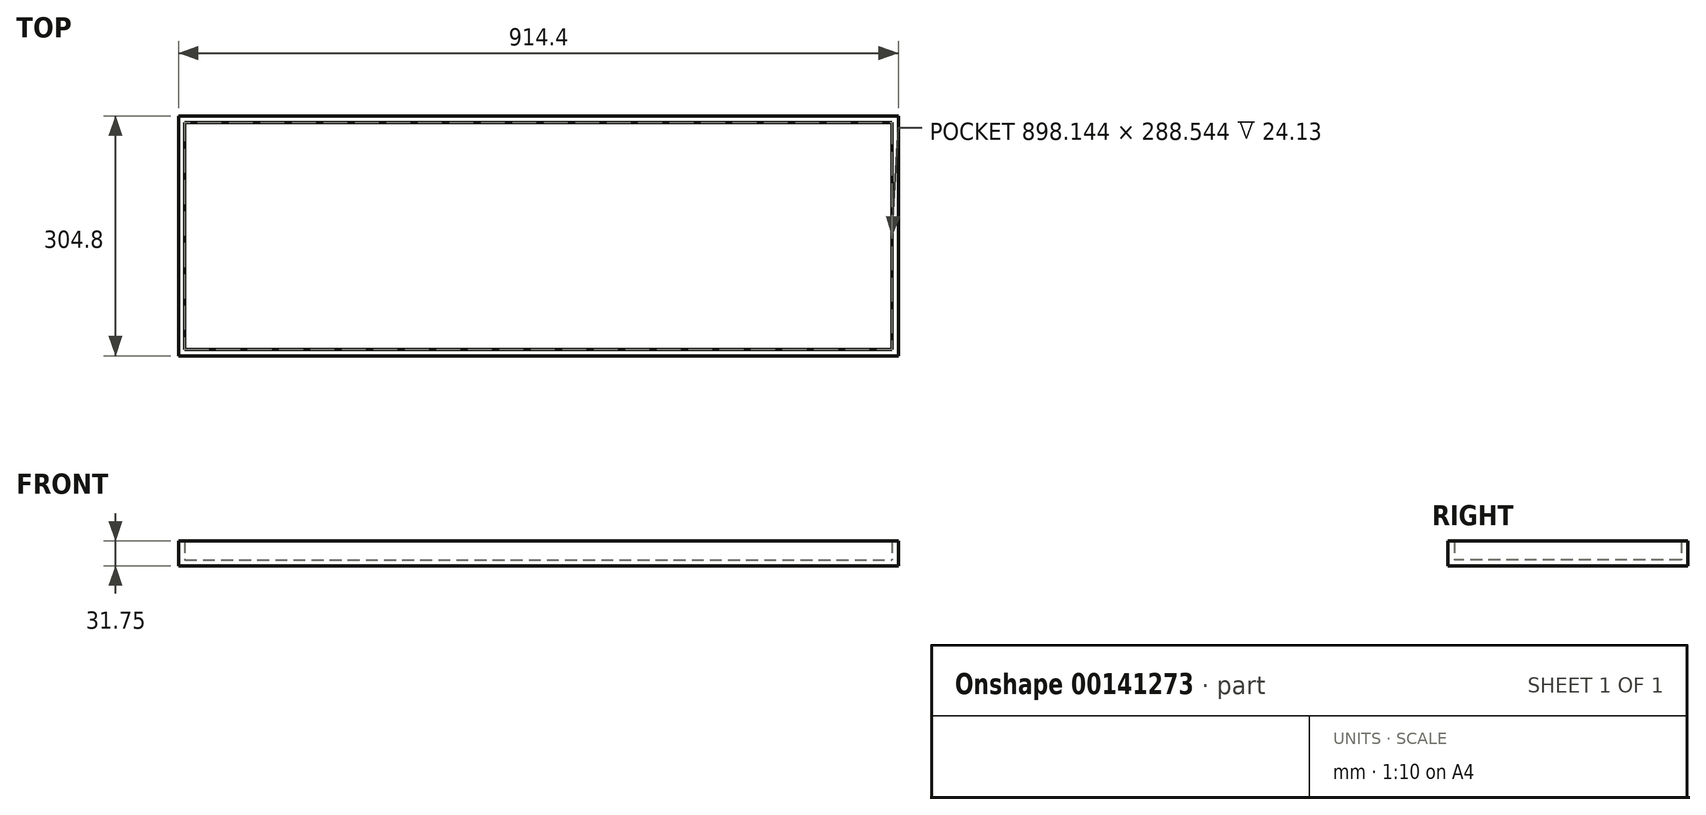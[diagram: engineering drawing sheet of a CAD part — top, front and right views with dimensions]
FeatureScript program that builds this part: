
annotation { "Feature Type Name" : "Feature", "Feature Type Description" : "" }
export const myFeature = defineFeature(function(context is Context, id is Id, definition is map)
    precondition{}
    {
        {
            var Q0;
            Q0=qCreatedBy(makeId("Top.planeOp"),FACE);
            var sketch = newSketch(context, id + "F0", { "sketchPlane" : qUnion([Q0])});
            skLineSegment(sketch, "E0.bottom", {"start": v(-457.2, 152.4) * mm, "end": v(457.2, 152.4) * mm});
            skLineSegment(sketch, "E0.top", {"start": v(-457.2, -152.4) * mm, "end": v(457.2, -152.4) * mm});
            skLineSegment(sketch, "E0.left", {"start": v(-457.2, 152.4) * mm, "end": v(-457.2, -152.4) * mm});
            skLineSegment(sketch, "E0.right", {"start": v(457.2, 152.4) * mm, "end": v(457.2, -152.4) * mm});
            skPoint(sketch, "E0.middle", {"position": v(0, 0) * mm});
            skSolve(sketch);
        }
        {
            var Q0;
            Q0 = qSketchRegion(id + "F0", true);
            extrude(context, id + "F1", {"entities" : qUnion([Q0]), "depth" : 7.62 * mm});
        }
        {
            var Q0;
            Q0=makeQuery(id+"F1.opExtrude","CAP_FACE",FACE,{"disambiguationData":[OSD([sQuery(id+"F0.wireOp",EDGE,"E0.bottom"),sQuery(id+"F0.wireOp",EDGE,"E0.top"),sQuery(id+"F0.wireOp",EDGE,"E0.left"),sQuery(id+"F0.wireOp",EDGE,"E0.right")])],"isStart":false});
            var sketch = newSketch(context, id + "F2", { "sketchPlane" : qUnion([Q0])});
            skLineSegment(sketch, "E1.0", {"start": v(-449.07, 144.27) * mm, "end": v(449.07, 144.27) * mm});
            skLineSegment(sketch, "E1.1", {"start": v(-449.07, 144.27) * mm, "end": v(-449.07, -144.27) * mm});
            skLineSegment(sketch, "E1.2", {"start": v(-449.07, -144.27) * mm, "end": v(449.07, -144.27) * mm});
            skLineSegment(sketch, "E1.3", {"start": v(449.07, 144.27) * mm, "end": v(449.07, -144.27) * mm});
            skLineSegment(sketch, "E2.0", {"start": v(-457.2, 152.4) * mm, "end": v(457.2, 152.4) * mm});
            skLineSegment(sketch, "E2.1", {"start": v(-457.2, 152.4) * mm, "end": v(-457.2, -152.4) * mm});
            skLineSegment(sketch, "E2.2", {"start": v(-457.2, -152.4) * mm, "end": v(457.2, -152.4) * mm});
            skLineSegment(sketch, "E2.3", {"start": v(457.2, 152.4) * mm, "end": v(457.2, -152.4) * mm});
            skSolve(sketch);
        }
        {
            var Q0;
            Q0=makeQuery(id+"F1.opExtrude","CAP_FACE",FACE,{"disambiguationData":[OSD([sQuery(id+"F0.wireOp",EDGE,"E0.bottom"),sQuery(id+"F0.wireOp",EDGE,"E0.top"),sQuery(id+"F0.wireOp",EDGE,"E0.left"),sQuery(id+"F0.wireOp",EDGE,"E0.right")])],"isStart":true});
            cPlane(context, id + "F3", {"entities" : qUnion([Q0]), "cplaneType" : CPlaneType.OFFSET, "offset" : 31.75 * mm, "oppositeDirection" : true, "width" : 152.4 * mm, "height" : 152.4 * mm});
        }
        {
            var Q0;
            Q0 = qSketchRegion(id + "F2", true);
            var Q1;
            Q1=qCreatedBy(id+"F3.planeOp",FACE);
            extrude(context, id + "F4", {"entities" : qUnion([Q0]), "operationType" : NewBodyOperationType.ADD, "endBound" : BoundingType.UP_TO_SURFACE, "endBoundEntityFace" : qUnion([Q1]), "depth" : 25.4 * mm});
        }
    });
